# Revit family: Electrical_Equipment-Floor_Box-Hubbell_Wiring-Single_Service_Two_Piece_Cover-PFB1
name_source: partatom
category: Electrical Fixtures
revit_build: Autodesk Revit 2015 (Build: 20140606_1530(x64)
units: mm (PartAtom-declared; Revit-internal decimal feet)

## types (1)
- Single Service Two Piece Covers
    Adapter Ring Part Number = PFBA1A
    Assembly Code = D5020115
    Can Material = Non_Metallic-Hubbell-Plastic
    Conduit Connector 1 Radius = 0' - 0 1/2"
    Conduit Connector 2 Radius = 0' - 0 3/8"
    Conduit Connector_1 Description = Conduit 1in. Connection
    Conduit Connector_2 Description = Conduit 1in. Connection
    Conduit Connector_3 Description = Conduit 0.75in. Connection
    Conduit Connector_4 Description = Conduit 0.75in. Connection
    Conduit Connector_5 Description = Y-Adapter 0.75in. Connection
    Conduit Connector_6 Description = Y-Adapter 0.75in. Connection
    Conduit Connector_7 Description = Y-Adapter 0.75in. Connection
    Conduit Connector_8 Description = Y-Adapter 0.75in. Connection
    Cover Material = Metal-Hubbell-Brass
    Default Elevation = 0' - 0"
    Description = Flush Round Single-Service Floor Box
    Low Voltage Divider Part Number = PFBT1A
    Manufacturer = Hubbell-Wiring
    Model = PFB1
    Product Documentation Link = http://ecatalog.hubbell-wiring.com
    Product Page URL = http://ecatalog.hubbell-wiring.com
    Product data url = https://bimobject.com
    Tile Ring Part Number = S5016
    URL = http://www.hubbell-wiring.com
    Void Radius = 0' - 2 1/16"
    Y-Adapter Part Number = PFBYA1

## geometry (parser evidence)
native form markers: Blend x54, Sweep x20
no freeform markers — native parametric forms only
